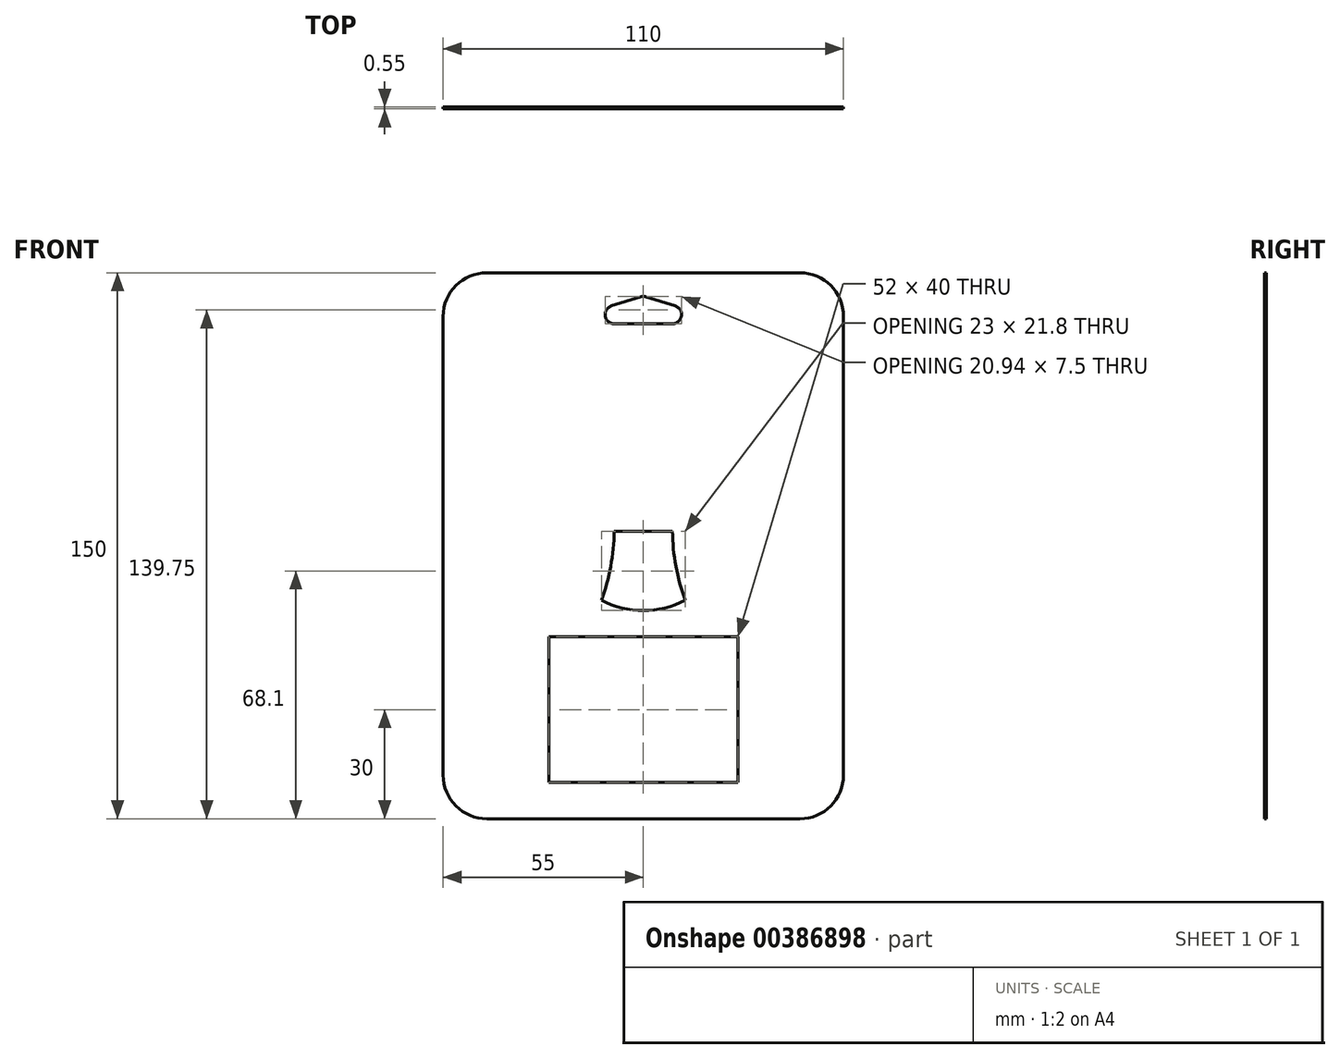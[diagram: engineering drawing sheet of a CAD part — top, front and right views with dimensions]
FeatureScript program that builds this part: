
annotation { "Feature Type Name" : "Feature", "Feature Type Description" : "" }
export const myFeature = defineFeature(function(context is Context, id is Id, definition is map)
    precondition{}
    {
        {
            var Q0;
            Q0=qCreatedBy(makeId("Front.planeOp"),FACE);
            var sketch = newSketch(context, id + "F0", { "sketchPlane" : qUnion([Q0])});
            skLineSegment(sketch, "E0.bottom", {"start": v(43, 75) * mm, "end": v(-43, 75) * mm});
            skLineSegment(sketch, "E0.top", {"start": v(43, -75) * mm, "end": v(-43, -75) * mm});
            skLineSegment(sketch, "E0.left", {"start": v(55, 63) * mm, "end": v(55, -63) * mm});
            skLineSegment(sketch, "E0.right", {"start": v(-55, 63) * mm, "end": v(-55, -63) * mm});
            skPoint(sketch, "E0.middle", {"position": v(0, 0) * mm});
            skPoint(sketch, "E1.visualSharp", {"position": v(-55, 75) * mm});
            skArc(sketch, "E1.filletArc", {"start": v(-43, 75) * mm, "mid": v(-51.49, 71.49) * mm, "end": v(-55, 63) * mm});
            skPoint(sketch, "E2.visualSharp", {"position": v(55, 75) * mm});
            skArc(sketch, "E2.filletArc", {"start": v(55, 63) * mm, "mid": v(51.49, 71.49) * mm, "end": v(43, 75) * mm});
            skPoint(sketch, "E3.visualSharp", {"position": v(55, -75) * mm});
            skArc(sketch, "E3.filletArc", {"start": v(43, -75) * mm, "mid": v(51.49, -71.49) * mm, "end": v(55, -63) * mm});
            skPoint(sketch, "E4.visualSharp", {"position": v(-55, -75) * mm});
            skArc(sketch, "E4.filletArc", {"start": v(-55, -63) * mm, "mid": v(-51.49, -71.49) * mm, "end": v(-43, -75) * mm});
            skSolve(sketch);
        }
        {
            var Q0;
            Q0=makeQuery(id+"F0.imprint","IMPRINT",FACE,{"disambiguationData":[TD([[makeQuery(id+"F0.imprint","IMPRINT",EDGE,{"derivedFrom":sQuery(id+"F0.wireOp",EDGE,"E0.bottom")}),1.0]])]});
            var Q1;
            Q1 = qSketchRegion(id + "F0", true);
            extrude(context, id + "F1", {"entities" : qUnion([Q0, Q1]), "depth" : 0.55 * mm, "offsetDistance" : 25 * mm});
        }
        {
            var Q0;
            Q0=qCreatedBy(makeId("Front.planeOp"),FACE);
            var sketch = newSketch(context, id + "F2", { "sketchPlane" : qUnion([Q0])});
            skLineSegment(sketch, "E5", {"start": v(-11.5, -15) * mm, "end": v(0, -15) * mm, "construction": true});
            skLineSegment(sketch, "E6", {"start": v(-8, 4) * mm, "end": v(0, 4) * mm});
            skArc(sketch, "E7", {"start": v(-11.5, -15) * mm, "mid": v(-5.92, -17.09) * mm, "end": v(0, -17.8) * mm});
            skLineSegment(sketch, "E8", {"start": v(0, 24.14) * mm, "end": v(0, 20.24) * mm, "construction": true});
            skLineSegment(sketch, "E9.MirrorCS", {"start": v(8, 4) * mm, "end": v(0, 4) * mm});
            skArc(sketch, "E10.MirrorCS", {"start": v(11.5, -15) * mm, "mid": v(5.92, -17.09) * mm, "end": v(0, -17.8) * mm});
            skLineSegment(sketch, "E11.bottom", {"start": v(26, -25) * mm, "end": v(-26, -25) * mm});
            skLineSegment(sketch, "E11.top", {"start": v(26, -65) * mm, "end": v(-26, -65) * mm});
            skLineSegment(sketch, "E11.left", {"start": v(26, -25) * mm, "end": v(26, -65) * mm});
            skLineSegment(sketch, "E11.right", {"start": v(-26, -25) * mm, "end": v(-26, -65) * mm});
            skPoint(sketch, "E11.middle", {"position": v(0, -45) * mm});
            skArc(sketch, "E12", {"start": v(-11.5, -15) * mm, "mid": v(-8.95, -5.65) * mm, "end": v(-8, 4) * mm});
            skArc(sketch, "E13.MirrorCS", {"start": v(11.5, -15) * mm, "mid": v(8.95, -5.65) * mm, "end": v(8, 4) * mm});
            skSolve(sketch);
        }
        {
            var Q0;
            Q0 = qSketchRegion(id + "F2", true);
            extrude(context, id + "F3", {"entities" : qUnion([Q0]), "operationType" : NewBodyOperationType.REMOVE, "endBound" : BoundingType.THROUGH_ALL, "depth" : 25 * mm, "offsetDistance" : 25 * mm});
        }
        {
            var Q0;
            Q0=qCreatedBy(makeId("Front.planeOp"),FACE);
            var sketch = newSketch(context, id + "F4", { "sketchPlane" : qUnion([Q0])});
            skLineSegment(sketch, "E14.bottom", {"start": v(8, 61) * mm, "end": v(-8, 61) * mm});
            skPoint(sketch, "E14.middle", {"position": v(0, 63.5) * mm});
            skArc(sketch, "E15", {"start": v(0.75, 68.39) * mm, "mid": v(0, 68.5) * mm, "end": v(-0.75, 68.39) * mm});
            skArc(sketch, "E16", {"start": v(-8.75, 65.89) * mm, "mid": v(-10.47, 63.12) * mm, "end": v(-8, 61) * mm});
            skPoint(sketch, "E16.first.point", {"position": v(-8, 66) * mm});
            skPoint(sketch, "E16.second.point", {"position": v(-10.5, 63.5) * mm});
            skPoint(sketch, "E16.third.point", {"position": v(-8, 61) * mm});
            skArc(sketch, "E17", {"start": v(8, 61) * mm, "mid": v(10.47, 63.12) * mm, "end": v(8.75, 65.89) * mm});
            skPoint(sketch, "E17.first.point", {"position": v(8, 66) * mm});
            skPoint(sketch, "E17.second.point", {"position": v(10.5, 63.5) * mm});
            skPoint(sketch, "E17.third.point", {"position": v(8, 61) * mm});
            skPoint(sketch, "E18.orphan", {"position": v(-10.5, 66) * mm});
            skPoint(sketch, "E19.orphan", {"position": v(-10.5, 61) * mm});
            skPoint(sketch, "E20.orphan", {"position": v(10.5, 61) * mm});
            skPoint(sketch, "E21.orphan", {"position": v(10.5, 66) * mm});
            skLineSegment(sketch, "E22", {"start": v(-8.75, 65.89) * mm, "end": v(-0.75, 68.39) * mm});
            skLineSegment(sketch, "E23", {"start": v(0.75, 68.39) * mm, "end": v(8.75, 65.89) * mm});
            skSolve(sketch);
        }
        {
            var Q0;
            Q0 = qSketchRegion(id + "F4", true);
            extrude(context, id + "F5", {"entities" : qUnion([Q0]), "operationType" : NewBodyOperationType.REMOVE, "endBound" : BoundingType.THROUGH_ALL, "depth" : 25 * mm, "offsetDistance" : 25 * mm});
        }
    });
